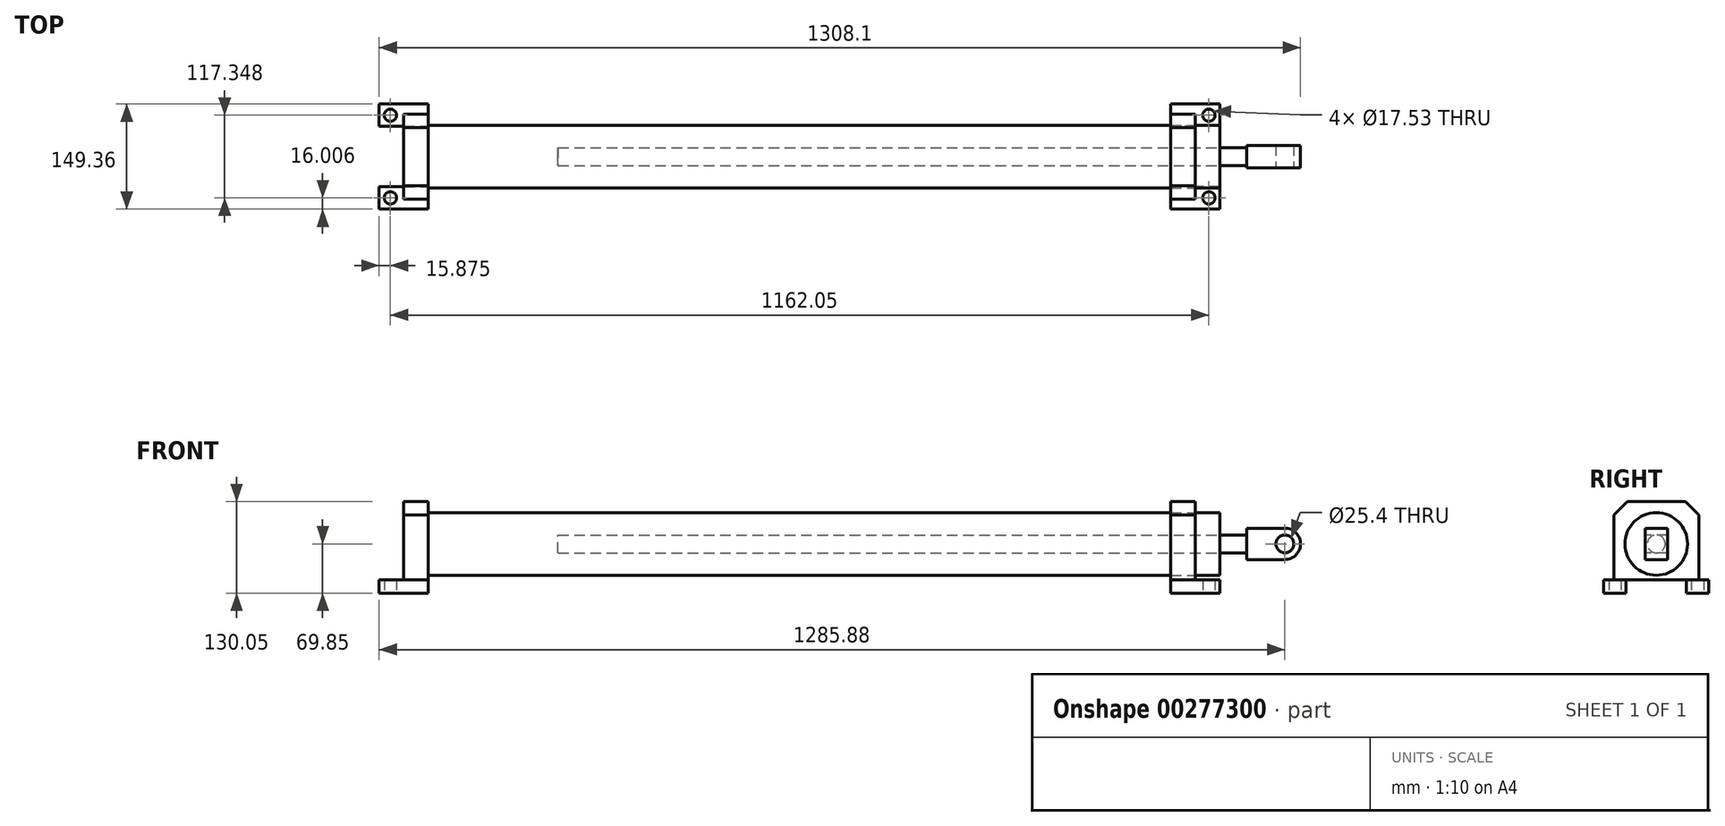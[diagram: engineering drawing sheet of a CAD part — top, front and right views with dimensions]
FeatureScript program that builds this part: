
annotation { "Feature Type Name" : "Feature", "Feature Type Description" : "" }
export const myFeature = defineFeature(function(context is Context, id is Id, definition is map)
    precondition{}
    {
        {
            var Q0;
            Q0=qCreatedBy(makeId("Top.planeOp"),FACE);
            var sketch = newSketch(context, id + "F0", { "sketchPlane" : qUnion([Q0])});
            skLineSegment(sketch, "E0.bottom", {"start": v(-596.9, 74.68) * mm, "end": v(596.9, 74.68) * mm, "construction": true});
            skLineSegment(sketch, "E0.top", {"start": v(-596.9, -74.68) * mm, "end": v(596.9, -74.68) * mm, "construction": true});
            skLineSegment(sketch, "E0.left", {"start": v(-596.9, 74.68) * mm, "end": v(-596.9, -74.68) * mm, "construction": true});
            skLineSegment(sketch, "E0.right", {"start": v(596.9, 74.68) * mm, "end": v(596.9, -74.68) * mm, "construction": true});
            skPoint(sketch, "E0.middle", {"position": v(0, 0) * mm});
            skLineSegment(sketch, "E1.bottom", {"start": v(-581.02, 58.67) * mm, "end": v(581.02, 58.67) * mm, "construction": true});
            skLineSegment(sketch, "E1.top", {"start": v(-581.02, -58.67) * mm, "end": v(581.02, -58.67) * mm, "construction": true});
            skLineSegment(sketch, "E1.left", {"start": v(-581.02, 58.67) * mm, "end": v(-581.02, -58.67) * mm, "construction": true});
            skLineSegment(sketch, "E1.right", {"start": v(581.02, 58.67) * mm, "end": v(581.02, -58.67) * mm, "construction": true});
            skLineSegment(sketch, "E2.bottom", {"start": v(-596.9, -74.68) * mm, "end": v(-527.05, -74.68) * mm});
            skLineSegment(sketch, "E2.top", {"start": v(-596.9, -42.93) * mm, "end": v(-527.05, -42.93) * mm});
            skLineSegment(sketch, "E2.left", {"start": v(-596.9, -74.68) * mm, "end": v(-596.9, -42.93) * mm});
            skLineSegment(sketch, "E2.right", {"start": v(-527.05, -74.68) * mm, "end": v(-527.05, -42.93) * mm});
            skCircle(sketch, "E3", {"center": v(-581.02, -58.67) * mm, "radius": 8.76 * mm});
            skSolve(sketch);
        }
        {
            var Q0;
            Q0 = qSketchRegion(id + "F0", true);
            extrude(context, id + "F1", {"entities" : qUnion([Q0]), "depth" : 19.05 * mm});
        }
        {
            var Q0;
            Q0=makeQuery(id+"F1.opExtrude","SWEPT_BODY",BODY,{"disambiguationData":[OSD([sQuery(id+"F0.wireOp",EDGE,"E2.bottom"),sQuery(id+"F0.wireOp",EDGE,"E2.top"),sQuery(id+"F0.wireOp",EDGE,"E2.left"),sQuery(id+"F0.wireOp",EDGE,"E2.right"),sQuery(id+"F0.wireOp",EDGE,"E3")])]});
            var Q1;
            Q1=qCreatedBy(makeId("Front.planeOp"),FACE);
            mirror(context, id + "F2", {"entities" : qUnion([Q0]), "mirrorPlane" : qUnion([Q1])});
        }
        {
            var Q0;
            Q0=makeQuery(id+"F2.opPattern","COPY",FACE,{"derivedFrom":makeQuery(id+"F1.opExtrude","CAP_FACE",FACE,{"disambiguationData":[OSD([sQuery(id+"F0.wireOp",EDGE,"E2.bottom"),sQuery(id+"F0.wireOp",EDGE,"E2.top"),sQuery(id+"F0.wireOp",EDGE,"E2.left"),sQuery(id+"F0.wireOp",EDGE,"E2.right"),sQuery(id+"F0.wireOp",EDGE,"E3")])],"isStart":false}),"instanceName":"1"});
            var sketch = newSketch(context, id + "F3", { "sketchPlane" : qUnion([Q0])});
            skLineSegment(sketch, "E4", {"start": v(-680.9, 0) * mm, "end": v(-408, 0) * mm, "construction": true});
            skLineSegment(sketch, "E5", {"start": v(-561.98, 74.68) * mm, "end": v(-561.98, -86.04) * mm, "construction": true});
            skPoint(sketch, "E5.endSnap0", {"position": v(-561.98, 42.93) * mm});
            skLineSegment(sketch, "E6.0", {"start": v(-680.9, -60.33) * mm, "end": v(-408, -60.33) * mm, "construction": true});
            skLineSegment(sketch, "E7.bottom", {"start": v(-561.98, -60.33) * mm, "end": v(-527.05, -60.33) * mm});
            skLineSegment(sketch, "E7.top", {"start": v(-561.98, 60.33) * mm, "end": v(-527.05, 60.33) * mm});
            skLineSegment(sketch, "E7.left", {"start": v(-561.98, -60.33) * mm, "end": v(-561.98, 60.33) * mm});
            skLineSegment(sketch, "E7.right", {"start": v(-527.05, -60.33) * mm, "end": v(-527.05, 60.33) * mm});
            skSolve(sketch);
        }
        {
            var Q0;
            Q0 = qSketchRegion(id + "F3", true);
            extrude(context, id + "F4", {"entities" : qUnion([Q0]), "depth" : 111 * mm});
        }
        {
            var Q0;
            Q0=makeQuery(id+"F4.opExtrude","CAP_EDGE",EDGE,{"disambiguationData":[OSD([sQuery(id+"F3.wireOp",EDGE,"E7.top")])],"isStart":false});
            var Q1;
            Q1=makeQuery(id+"F4.opExtrude","CAP_EDGE",EDGE,{"disambiguationData":[OSD([sQuery(id+"F3.wireOp",EDGE,"E7.bottom")])],"isStart":false});
            chamfer(context, id + "F5", {"entities" : qUnion([Q0, Q1]), "width" : 19.05 * mm, "tangentPropagation" : true});
        }
        {
            var Q0;
            Q0=makeQuery(id+"F4.opExtrude","SWEPT_BODY",BODY,{"disambiguationData":[OSD([sQuery(id+"F3.wireOp",EDGE,"E7.bottom"),sQuery(id+"F3.wireOp",EDGE,"E7.top"),sQuery(id+"F3.wireOp",EDGE,"E7.left"),sQuery(id+"F3.wireOp",EDGE,"E7.right")])]});
            var Q1;
            Q1=makeQuery(id+"F2.opPattern","COPY",BODY,{"derivedFrom":makeQuery(id+"F1.opExtrude","SWEPT_BODY",BODY,{"disambiguationData":[OSD([sQuery(id+"F0.wireOp",EDGE,"E2.bottom"),sQuery(id+"F0.wireOp",EDGE,"E2.top"),sQuery(id+"F0.wireOp",EDGE,"E2.left"),sQuery(id+"F0.wireOp",EDGE,"E2.right"),sQuery(id+"F0.wireOp",EDGE,"E3")])]}),"instanceName":"1"});
            var Q2;
            Q2=makeQuery(id+"F1.opExtrude","SWEPT_BODY",BODY,{"disambiguationData":[OSD([sQuery(id+"F0.wireOp",EDGE,"E2.bottom"),sQuery(id+"F0.wireOp",EDGE,"E2.top"),sQuery(id+"F0.wireOp",EDGE,"E2.left"),sQuery(id+"F0.wireOp",EDGE,"E2.right"),sQuery(id+"F0.wireOp",EDGE,"E3")])]});
            booleanBodies(context, id + "F6", {"operationType" : BooleanOperationType.UNION, "tools" : qUnion([Q0, Q1, Q2])});
        }
        {
            var Q0;
            Q0=makeQuery(id+"F4.opExtrude","SWEPT_BODY",BODY,{"disambiguationData":[OSD([sQuery(id+"F3.wireOp",EDGE,"E7.bottom"),sQuery(id+"F3.wireOp",EDGE,"E7.top"),sQuery(id+"F3.wireOp",EDGE,"E7.left"),sQuery(id+"F3.wireOp",EDGE,"E7.right")])]});
            var Q1;
            Q1=qCreatedBy(makeId("Right.planeOp"),FACE);
            mirror(context, id + "F7", {"entities" : qUnion([Q0]), "mirrorPlane" : qUnion([Q1])});
        }
        {
            var Q0;
            Q0=makeQuery(id+"F7.opPattern","COPY",FACE,{"derivedFrom":makeQuery(id+"F1.opExtrude","SWEPT_FACE",FACE,{"disambiguationData":[OSD([sQuery(id+"F0.wireOp",EDGE,"E2.left")])]}),"instanceName":"1"});
            var sketch = newSketch(context, id + "F8", { "sketchPlane" : qUnion([Q0])});
            skLineSegment(sketch, "E8", {"start": v(0, 0) * mm, "end": v(0, 69.85) * mm, "construction": true});
            skCircle(sketch, "E9", {"center": v(0, 69.85) * mm, "radius": 44.45 * mm});
            skSolve(sketch);
        }
        {
            var Q0;
            Q0 = qSketchRegion(id + "F8", true);
            var Q1;
            {var subQ0=makeQuery(id+"F1.opExtrude","SWEPT_FACE",FACE,{"disambiguationData":[OSD([sQuery(id+"F0.wireOp",EDGE,"E2.right")])]});Q1=makeQuery(id+"F6.opBoolean","MERGE",FACE,{"derivedFrom":[subQ0,makeQuery(id+"F2.opPattern","COPY",FACE,{"derivedFrom":subQ0,"instanceName":"1"}),makeQuery(id+"F4.opExtrude","SWEPT_FACE",FACE,{"disambiguationData":[OSD([sQuery(id+"F3.wireOp",EDGE,"E7.right")])]})]});}
            extrude(context, id + "F9", {"entities" : qUnion([Q0]), "endBound" : BoundingType.UP_TO_SURFACE, "oppositeDirection" : true, "endBoundEntityFace" : qUnion([Q1]), "depth" : 25.4 * mm});
        }
        {
            var Q0;
            Q0=makeQuery(id+"F9.opExtrude","CAP_FACE",FACE,{"disambiguationData":[OSD([sQuery(id+"F8.wireOp",EDGE,"E9")])],"isStart":true});
            cPlane(context, id + "F10", {"entities" : qUnion([Q0]), "cplaneType" : CPlaneType.OFFSET, "offset" : 76.2 * mm, "width" : 152.4 * mm, "height" : 152.4 * mm});
        }
        {
            var Q0;
            Q0=qCreatedBy(id+"F10.planeOp",FACE);
            var sketch = newSketch(context, id + "F11", { "sketchPlane" : qUnion([Q0])});
            skCircle(sketch, "E10.0", {"center": v(0, 69.85) * mm, "radius": 44.45 * mm, "construction": true});
            skCircle(sketch, "E11", {"center": v(0, 69.85) * mm, "radius": 12.7 * mm});
            skSolve(sketch);
        }
        {
            var Q0;
            Q0 = qSketchRegion(id + "F11", true);
            extrude(context, id + "F12", {"entities" : qUnion([Q0]), "oppositeDirection" : true, "depth" : 1016 * mm});
        }
        {
            var Q0;
            Q0=qCreatedBy(id+"F10.planeOp",FACE);
            cPlane(context, id + "F13", {"entities" : qUnion([Q0]), "cplaneType" : CPlaneType.OFFSET, "offset" : 38.1 * mm, "oppositeDirection" : true, "width" : 152.4 * mm, "height" : 152.4 * mm});
        }
        {
            var Q0;
            Q0=qCreatedBy(id+"F13.planeOp",FACE);
            var sketch = newSketch(context, id + "F14", { "sketchPlane" : qUnion([Q0])});
            skCircle(sketch, "E12.0", {"center": v(0, 69.85) * mm, "radius": 12.7 * mm, "construction": true});
            skLineSegment(sketch, "E13.bottom", {"start": v(-15.88, 92.08) * mm, "end": v(15.88, 92.08) * mm});
            skLineSegment(sketch, "E13.top", {"start": v(-15.88, 47.63) * mm, "end": v(15.87, 47.63) * mm});
            skLineSegment(sketch, "E13.left", {"start": v(-15.88, 92.08) * mm, "end": v(-15.88, 47.63) * mm});
            skLineSegment(sketch, "E13.right", {"start": v(15.88, 92.08) * mm, "end": v(15.87, 47.63) * mm});
            skSolve(sketch);
        }
        {
            var Q0;
            Q0 = qSketchRegion(id + "F14", true);
            extrude(context, id + "F15", {"entities" : qUnion([Q0]), "operationType" : NewBodyOperationType.ADD, "depth" : 76.2 * mm});
        }
        {
            var Q0;
            Q0=makeQuery(id+"F15.opExtrude","CAP_EDGE",EDGE,{"disambiguationData":[OSD([sQuery(id+"F14.wireOp",EDGE,"E13.bottom")])],"isStart":false});
            var Q1;
            Q1=makeQuery(id+"F15.opExtrude","CAP_EDGE",EDGE,{"disambiguationData":[OSD([sQuery(id+"F14.wireOp",EDGE,"E13.top")])],"isStart":false});
            fillet(context, id + "F16", {"entities" : qUnion([Q0, Q1]), "radius" : 22.22 * mm, "tangentPropagation" : true, "allowEdgeOverflow" : false});
        }
        {
            var Q0;
            Q0=makeQuery(id+"F15.opExtrude","SWEPT_FACE",FACE,{"disambiguationData":[OSD([sQuery(id+"F14.wireOp",EDGE,"E13.left")])]});
            var sketch = newSketch(context, id + "F17", { "sketchPlane" : qUnion([Q0])});
            skArc(sketch, "E14.0", {"start": v(688.98, 47.63) * mm, "mid": v(711.2, 69.85) * mm, "end": v(688.98, 92.08) * mm, "construction": true});
            skSolve(sketch);
        }
        {
            var Q0;
            Q0=sQuery(id+"F17.wireOp",VERTEX,"E14.0.center");
            var Q1;
            Q1=makeQuery(id+"F12.opExtrude","SWEPT_BODY",BODY,{"disambiguationData":[OSD([sQuery(id+"F11.wireOp",EDGE,"E11")])]});
            hole(context, id + "F18", {"style" : HoleStyle.SIMPLE, "endStyle" : HoleEndStyle.THROUGH, "standardTappedOrClearance" : lookupTablePath({ "standard" : "ANSI", "size" : "1 (1)", "type" : "Drilled" }), "standardBlindInLast" : lookupTablePath({ "standard" : "ANSI", "size" : "1", "type" : "Drilled" }), "holeDiameter" : 25.4 * mm, "tappedDepth" : 8.9 * mm, "tapClearance" : 3, "startFromSketch" : true, "locations" : qUnion([Q0]), "scope" : qUnion([Q1])});
        }
    });
